# Revit family: ArandelaConcreto_ARC5W_PowerLume
name_source: partatom
category: Luminárias
units: mm (PartAtom-declared; Revit-internal decimal feet)

## family parameters
Compartilhado = Sim
Corte com vazios quando carregada = Sim
Cota do conector redondo = Utilizar diâmetro
Fonte luminosa = Não
Hospedeiro = Face
Manter orientação da anotação = Não
Número OmniClass = 23.80.70.14.11.17
Ponto de cálculo do ambiente = Não
Tipo de parte = Normal
Título OmniClass = Wall or Ceiling Mounted External Lighting

## types (1)
- ARC5W
    Altura = 170 mm  [stored 0.557743 ft]
    Carga Aparente Luminária = 0 VA
    Catálogo de produtos = https://www.powerlume.com.br
    Comentários de voltagem = 110 ou 220Vac 50/60Hz com driver incorporado
    Contato do fabricante = (54) 3066-6488
    Data da atualização = 27/02/2025
    Descrição = Arandela de sobrepor LED facho direto em concreto
    Elevação-padrão = 1219 mm
    Fabricante = Power Lume
    Fator de Potência Luminária = 1
    Fluxo luminoso = 585 lm
    Frame = Concreto, leve
    IP = 65
    IRC = 90
    IfcExportAs = IfcLightFixtureType
    Largura = 110 mm  [stored 0.360892 ft]
    Localização = Caxias do Sul - RS / Brasil
    Lâmpada = Placa LED
    Modelo = ARC5W
    Peso = 0
    Potência = 5W
    Profundidade = 135 mm  [stored 0.442913 ft]
    Refletor = Metal - Alumínio
    Temperatura de cor = 3000K
    Tipo de imagem = FOTO ARC5W.png
    URL = https://www.powerlume.com.br
    URL do produto = https://www.powerlume.com.br
    Versão = 1
    Vida útil = 60000h
    Voltagem Luminária = 0 V
    Ângulo de abertura = 80°

note: [stored X ft] marks values corroborated as IEEE doubles in the binary element streams (Revit-internal decimal feet)
